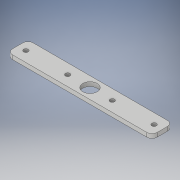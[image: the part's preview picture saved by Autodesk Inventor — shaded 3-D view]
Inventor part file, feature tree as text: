
AUTODESK INVENTOR PART (.ipt)
format: ipt  version: 2018 (Build 220112000, 112)  size: 136,704 bytes
history: native  units: in
note: dims shown in document units (in); Inventor stores cm internally (conversion verified against a paired STEP export)
features: sketch x6, hole x4, extrude x2, fillet x1
ambient origin geometry x8: Origin, YZ Plane, XZ Plane, XY Plane, X Axis, Y Axis, Z Axis, Center Point
bodies: Solid1 (feature_tree)
feature tree (13):
  extrude  "Extrusion1"  Depth=0.5in
  fillet  "Fillet1"  Radius=0.1in
  extrude  "Extrusion2"  Depth=0.125in
  hole  "Hole1"  [1 undecoded]
  hole  "Hole2"  [1 undecoded]
  hole  "Hole3"  [1 undecoded]
  hole  "Hole4"  [1 undecoded]
  sketch  "Sketch1"  dims[d0=3.5in d1=0.5in d2=0.1in d3=0.0in]
  sketch  "Sketch2"  dims[d4=0.125in d5=1.75in]
  sketch  "Sketch3"  dims[d6=0.35in d7=0.1in d8=0.0in]
  sketch  "Sketch4"  dims[d9=0.54in]
  sketch  "Sketch5"  dims[d10=0.11in d11=0.75in d12=0.375in d13=0.25in d14=0.5635in d15=1.0in d16=0.8108in d17=0.54in]
  sketch  "Sketch6"  dims[d18=0.11in d19=0.75in d20=0.375in d21=0.25in d22=0.5635in d23=1.0in d24=0.8108in d25=0.2in d26=0.11in d27=0.75in d28=0.375in d29=0.25in d30=0.5635in d31=1.0in d32=0.8108in d33=0.2in d34=0.11in d35=0.75in d36=0.375in d37=0.25in d38=0.5635in d39=1.0in d40=0.8108in]
note: 4 required parameter values undecoded (feature->parameter linkage not recoverable at this tier; creation-order binding heuristic only, values carry confidence <= 0.55)
